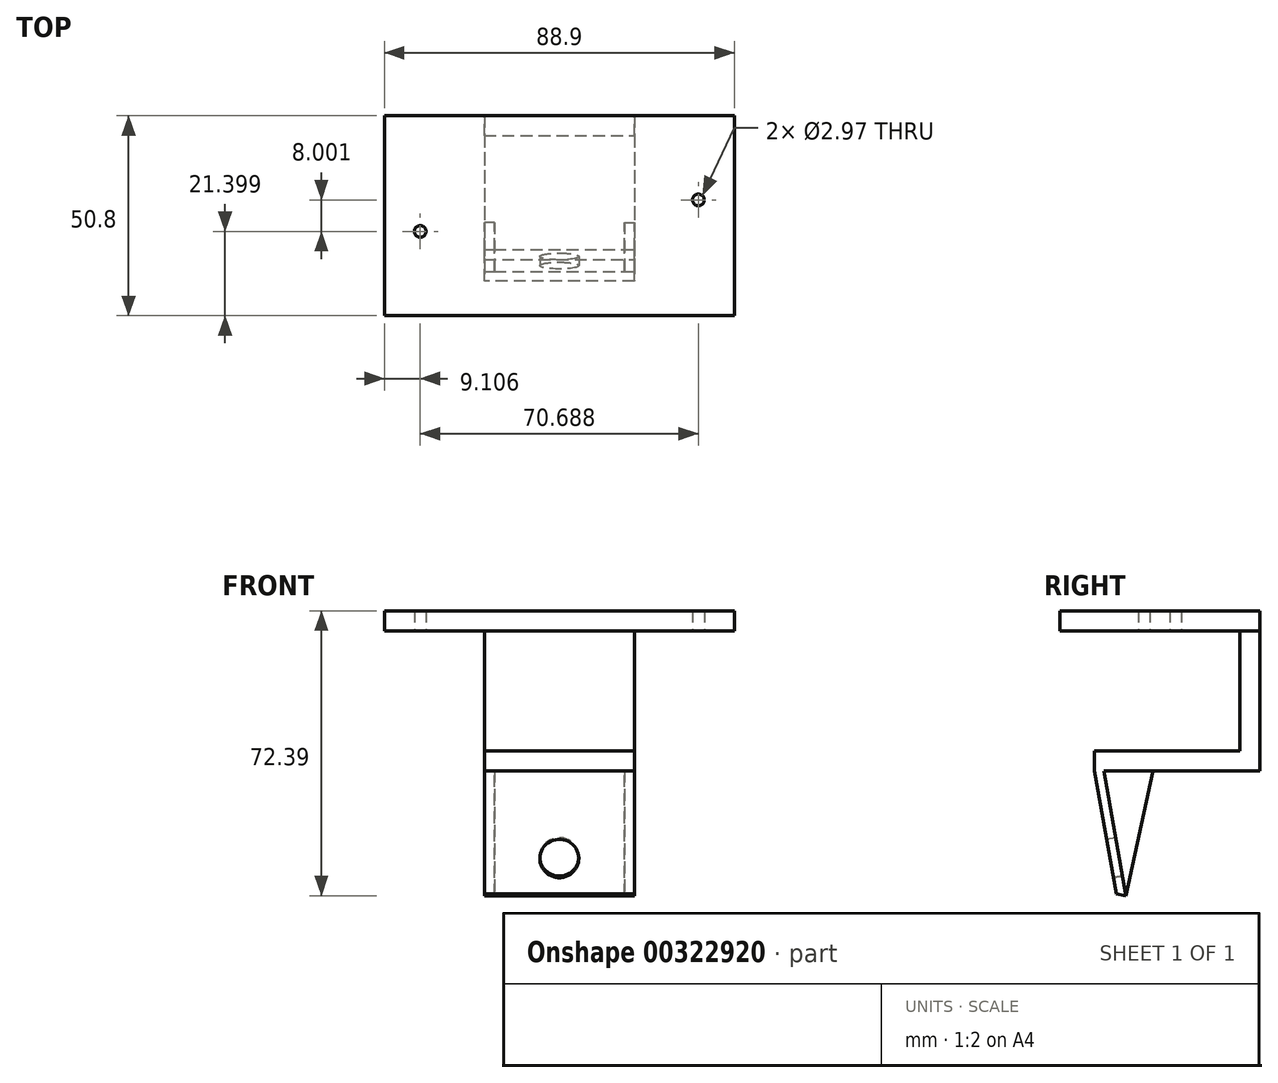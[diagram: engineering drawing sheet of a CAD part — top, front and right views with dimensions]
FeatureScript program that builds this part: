
annotation { "Feature Type Name" : "Feature", "Feature Type Description" : "" }
export const myFeature = defineFeature(function(context is Context, id is Id, definition is map)
    precondition{}
    {
        {
            var Q0;
            Q0=qCreatedBy(makeId("Top.planeOp"),FACE);
            var sketch = newSketch(context, id + "F0", { "sketchPlane" : qUnion([Q0])});
            skLineSegment(sketch, "E0.bottom", {"start": v(-37.88, 19.27) * mm, "end": v(37.88, 19.27) * mm});
            skLineSegment(sketch, "E0.top", {"start": v(-37.88, -19.27) * mm, "end": v(37.88, -19.27) * mm});
            skLineSegment(sketch, "E0.left", {"start": v(-37.88, 19.27) * mm, "end": v(-37.88, -19.27) * mm});
            skLineSegment(sketch, "E0.right", {"start": v(37.88, 19.27) * mm, "end": v(37.88, -19.27) * mm});
            skPoint(sketch, "E0.middle", {"position": v(0, 0) * mm});
            skSolve(sketch);
        }
        {
            var Q0;
            Q0=qCreatedBy(makeId("Top.planeOp"),FACE);
            var sketch = newSketch(context, id + "F1", { "sketchPlane" : qUnion([Q0])});
            skLineSegment(sketch, "E1.bottom", {"start": v(-44.45, 25.4) * mm, "end": v(44.45, 25.4) * mm});
            skLineSegment(sketch, "E1.top", {"start": v(-44.45, -25.4) * mm, "end": v(44.45, -25.4) * mm});
            skLineSegment(sketch, "E1.left", {"start": v(-44.45, 25.4) * mm, "end": v(-44.45, -25.4) * mm});
            skLineSegment(sketch, "E1.right", {"start": v(44.45, 25.4) * mm, "end": v(44.45, -25.4) * mm});
            skPoint(sketch, "E1.middle", {"position": v(0, 0) * mm});
            skCircle(sketch, "E2", {"center": v(35.34, 4) * mm, "radius": 1.49 * mm});
            skCircle(sketch, "E3", {"center": v(-35.34, -4) * mm, "radius": 1.49 * mm});
            skSolve(sketch);
        }
        {
            var Q0;
            Q0=makeQuery(id+"F1.imprint","IMPRINT",FACE,{"disambiguationData":[TD([[makeQuery(id+"F1.imprint","IMPRINT",EDGE,{"derivedFrom":sQuery(id+"F1.wireOp",EDGE,"E1.bottom")}),-1.0]])]});
            extrude(context, id + "F2", {"entities" : qUnion([Q0]), "depth" : 5.08 * mm});
        }
        {
            var Q0;
            Q0=makeQuery(id+"F2.opExtrude","CAP_FACE",FACE,{"disambiguationData":[OSD([sQuery(id+"F1.wireOp",EDGE,"E1.bottom"),sQuery(id+"F1.wireOp",EDGE,"E1.top"),sQuery(id+"F1.wireOp",EDGE,"E1.left"),sQuery(id+"F1.wireOp",EDGE,"E1.right"),sQuery(id+"F1.wireOp",EDGE,"E2"),sQuery(id+"F1.wireOp",EDGE,"E3")])],"isStart":true});
            var sketch = newSketch(context, id + "F3", { "sketchPlane" : qUnion([Q0])});
            skLineSegment(sketch, "E4.bottom", {"start": v(-19.05, -20.32) * mm, "end": v(19.05, -20.32) * mm});
            skLineSegment(sketch, "E4.top", {"start": v(-19.05, -30.48) * mm, "end": v(19.05, -30.48) * mm});
            skLineSegment(sketch, "E4.left", {"start": v(-19.05, -20.32) * mm, "end": v(-19.05, -30.48) * mm});
            skLineSegment(sketch, "E4.right", {"start": v(19.05, -20.32) * mm, "end": v(19.05, -30.48) * mm});
            skPoint(sketch, "E4.middle", {"position": v(0, -25.4) * mm});
            skSolve(sketch);
        }
        {
            var Q0;
            {var subQ0=sQuery(id+"F3.wireOp",EDGE,"E4.bottom");Q0=makeQuery(id+"F3.imprint","IMPRINT",FACE,{"disambiguationData":[TD([[makeQuery(id+"F3.imprint","IMPRINT",EDGE,{"derivedFrom":subQ0}),-1.0]])]});}
            extrude(context, id + "F4", {"entities" : qUnion([Q0]), "operationType" : NewBodyOperationType.ADD, "depth" : 30.48 * mm});
        }
        {
            var Q0;
            Q0=makeQuery(id+"F4.opExtrude","CAP_FACE",FACE,{"disambiguationData":[OSD([sQuery(id+"F1.wireOp",EDGE,"E1.bottom"),sQuery(id+"F3.wireOp",EDGE,"E4.bottom"),sQuery(id+"F3.wireOp",EDGE,"E4.left"),sQuery(id+"F3.wireOp",EDGE,"E4.right")])],"isStart":false});
            var sketch = newSketch(context, id + "F5", { "sketchPlane" : qUnion([Q0])});
            skLineSegment(sketch, "E5.bottom", {"start": v(19.05, -25.4) * mm, "end": v(-19.05, -25.4) * mm});
            skLineSegment(sketch, "E5.top", {"start": v(19.05, 16.6) * mm, "end": v(-19.05, 16.6) * mm});
            skLineSegment(sketch, "E5.left", {"start": v(19.05, -25.4) * mm, "end": v(19.05, 16.6) * mm});
            skLineSegment(sketch, "E5.right", {"start": v(-19.05, -25.4) * mm, "end": v(-19.05, 16.6) * mm});
            skSolve(sketch);
        }
        {
            var Q0;
            {var subQ3=sQuery(id+"F5.wireOp",EDGE,"E5.top");Q0=makeQuery(id+"F5.imprint","IMPRINT",FACE,{"disambiguationData":[TD([[makeQuery(id+"F5.imprint","IMPRINT",EDGE,{"derivedFrom":subQ3}),1.0]])]});}
            var Q1;
            {var subQ4=makeQuery(id+"F4.opExtrude","CAP_EDGE",EDGE,{"disambiguationData":[OSD([sQuery(id+"F3.wireOp",EDGE,"E4.bottom")])],"isStart":false});Q1=makeQuery(id+"F5.imprint","IMPRINT",FACE,{"disambiguationData":[TD([[makeQuery(id+"F5.imprint","IMPRINT",EDGE,{"derivedFrom":subQ4}),-1.0]])]});}
            extrude(context, id + "F6", {"entities" : qUnion([Q0, Q1]), "operationType" : NewBodyOperationType.ADD, "depth" : 5.08 * mm});
        }
        {
            var Q0;
            Q0=makeQuery(id+"F6.boolean.opBoolean","MERGE",FACE,{"derivedFrom":[makeQuery(id+"F4.opExtrude","SWEPT_FACE",FACE,{"disambiguationData":[OSD([sQuery(id+"F3.wireOp",EDGE,"E4.right")])]}),makeQuery(id+"F6.opExtrude","SWEPT_FACE",FACE,{"disambiguationData":[OSD([sQuery(id+"F5.wireOp",EDGE,"E5.left")])]})]});
            var sketch = newSketch(context, id + "F7", { "sketchPlane" : qUnion([Q0])});
            skLineSegment(sketch, "E6", {"start": v(-16.6, -35.56) * mm, "end": v(-11.1, -66.77) * mm});
            skLineSegment(sketch, "E7", {"start": v(-14.22, -35.56) * mm, "end": v(-8.62, -67.31) * mm});
            skLineSegment(sketch, "E8", {"start": v(-11.1, -66.77) * mm, "end": v(-8.62, -67.31) * mm});
            skLineSegment(sketch, "E9", {"start": v(-16.6, -35.56) * mm, "end": v(-14.22, -35.56) * mm});
            skSolve(sketch);
        }
        {
            var Q0;
            Q0 = qSketchRegion(id + "F7", true);
            extrude(context, id + "F8", {"entities" : qUnion([Q0]), "oppositeDirection" : true, "depth" : 38.1 * mm});
        }
        {
            var Q0;
            Q0=makeQuery(id+"F8.opExtrude","SWEPT_FACE",FACE,{"disambiguationData":[OSD([sQuery(id+"F7.wireOp",EDGE,"E6")])]});
            var sketch = newSketch(context, id + "F9", { "sketchPlane" : qUnion([Q0])});
            skLineSegment(sketch, "E10", {"start": v(29.05, -47.95) * mm, "end": v(-57.11, -47.95) * mm});
            skLineSegment(sketch, "E11", {"start": v(0, -27.36) * mm, "end": v(0, -68.72) * mm});
            skPoint(sketch, "E11.endSnap0", {"position": v(0, -32.14) * mm});
            skPoint(sketch, "E12", {"position": v(0, -54.76) * mm});
            skCircle(sketch, "E13", {"center": v(0, -54.76) * mm, "radius": 4.95 * mm});
            skSolve(sketch);
        }
        {
            var Q0;
            Q0=sQuery(id+"F9.wireOp",VERTEX,"E12");
            var Q1;
            Q1=makeQuery(id+"F8.opExtrude","SWEPT_BODY",BODY,{"disambiguationData":[OSD([sQuery(id+"F7.wireOp",EDGE,"E6"),sQuery(id+"F7.wireOp",EDGE,"E7"),sQuery(id+"F7.wireOp",EDGE,"E8"),sQuery(id+"F7.wireOp",EDGE,"E9")])]});
            hole(context, id + "F10", {"style" : HoleStyle.SIMPLE, "endStyle" : HoleEndStyle.THROUGH, "holeDiameter" : 9.9 * mm, "tappedDepth" : 12.7 * mm, "tapClearance" : 3, "locations" : qUnion([Q0]), "scope" : qUnion([Q1])});
        }
        {
            var Q0;
            Q0=makeQuery(id+"F8.opExtrude","CAP_FACE",FACE,{"disambiguationData":[OSD([sQuery(id+"F7.wireOp",EDGE,"E6"),sQuery(id+"F7.wireOp",EDGE,"E7"),sQuery(id+"F7.wireOp",EDGE,"E8"),sQuery(id+"F7.wireOp",EDGE,"E9")])],"isStart":true});
            var sketch = newSketch(context, id + "F11", { "sketchPlane" : qUnion([Q0])});
            skLineSegment(sketch, "E14", {"start": v(-8.62, -67.31) * mm, "end": v(-1.71, -35.76) * mm});
            skLineSegment(sketch, "E15", {"start": v(-1.71, -35.76) * mm, "end": v(-14.22, -35.56) * mm});
            skLineSegment(sketch, "E16", {"start": v(-14.22, -35.56) * mm, "end": v(-8.62, -67.31) * mm});
            skSolve(sketch);
        }
        {
            var Q0;
            Q0=makeQuery(id+"F11.imprint","IMPRINT",FACE,{"disambiguationData":[TD([[makeQuery(id+"F11.imprint","IMPRINT",EDGE,{"derivedFrom":sQuery(id+"F11.wireOp",EDGE,"E14")}),1.0]])]});
            extrude(context, id + "F12", {"entities" : qUnion([Q0]), "oppositeDirection" : true, "depth" : 2.54 * mm});
        }
        {
            var Q0;
            Q0=makeQuery(id+"F8.opExtrude","CAP_FACE",FACE,{"disambiguationData":[OSD([sQuery(id+"F7.wireOp",EDGE,"E6"),sQuery(id+"F7.wireOp",EDGE,"E7"),sQuery(id+"F7.wireOp",EDGE,"E8"),sQuery(id+"F7.wireOp",EDGE,"E9")])],"isStart":false});
            var sketch = newSketch(context, id + "F13", { "sketchPlane" : qUnion([Q0])});
            skLineSegment(sketch, "E17", {"start": v(8.62, -67.31) * mm, "end": v(1.68, -35.63) * mm});
            skLineSegment(sketch, "E18", {"start": v(1.68, -35.63) * mm, "end": v(14.22, -35.56) * mm});
            skLineSegment(sketch, "E19", {"start": v(14.22, -35.56) * mm, "end": v(8.62, -67.31) * mm});
            skSolve(sketch);
        }
        {
            var Q0;
            Q0 = qSketchRegion(id + "F13", true);
            extrude(context, id + "F14", {"entities" : qUnion([Q0]), "operationType" : NewBodyOperationType.ADD, "oppositeDirection" : true, "depth" : 2.54 * mm});
        }
    });
